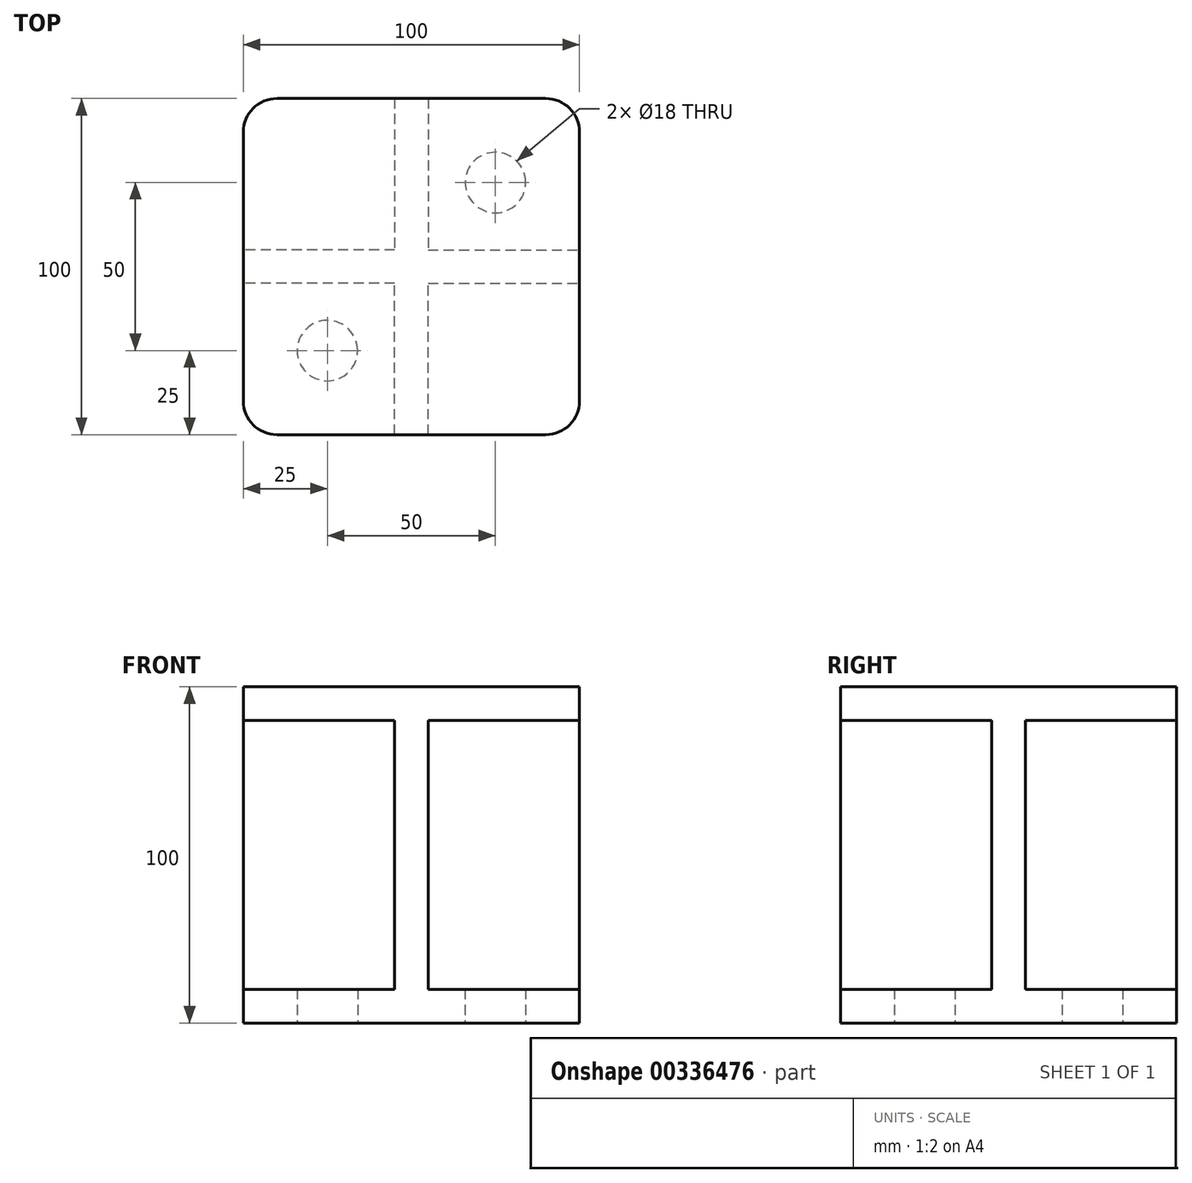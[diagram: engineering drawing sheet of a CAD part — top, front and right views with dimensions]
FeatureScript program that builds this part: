
annotation { "Feature Type Name" : "Feature", "Feature Type Description" : "" }
export const myFeature = defineFeature(function(context is Context, id is Id, definition is map)
    precondition{}
    {
        {
            var Q0;
            Q0=qCreatedBy(makeId("Top.planeOp"),FACE);
            var sketch = newSketch(context, id + "F0", { "sketchPlane" : qUnion([Q0])});
            skLineSegment(sketch, "E0", {"start": v(0, -50) * mm, "end": v(5, -50) * mm});
            skLineSegment(sketch, "E1", {"start": v(5, -50) * mm, "end": v(5, -5) * mm});
            skLineSegment(sketch, "E2", {"start": v(5, -5) * mm, "end": v(50, -5) * mm});
            skLineSegment(sketch, "E3", {"start": v(50, -5) * mm, "end": v(50, 0) * mm});
            skLineSegment(sketch, "E4.MirrorCS", {"start": v(50, 5) * mm, "end": v(50, 0) * mm});
            skLineSegment(sketch, "E5.MirrorCS", {"start": v(5, 5) * mm, "end": v(50, 5) * mm});
            skLineSegment(sketch, "E6.MirrorCS", {"start": v(5, 50) * mm, "end": v(5, 5) * mm});
            skLineSegment(sketch, "E7.MirrorCS", {"start": v(0, 50) * mm, "end": v(5, 50) * mm});
            skLineSegment(sketch, "E8.MirrorCS", {"start": v(0, 50) * mm, "end": v(-5, 50) * mm});
            skLineSegment(sketch, "E9.MirrorCS", {"start": v(-5, 50) * mm, "end": v(-5, 5) * mm});
            skLineSegment(sketch, "E10.MirrorCS", {"start": v(-5, 5) * mm, "end": v(-50, 5) * mm});
            skLineSegment(sketch, "E11.MirrorCS", {"start": v(-50, 5) * mm, "end": v(-50, 0) * mm});
            skLineSegment(sketch, "E12.MirrorCS", {"start": v(-50, -5) * mm, "end": v(-50, 0) * mm});
            skLineSegment(sketch, "E13.MirrorCS", {"start": v(-5, -5) * mm, "end": v(-50, -5) * mm});
            skLineSegment(sketch, "E14.MirrorCS", {"start": v(-5, -50) * mm, "end": v(-5, -5) * mm});
            skLineSegment(sketch, "E15.MirrorCS", {"start": v(0, -50) * mm, "end": v(-5, -50) * mm});
            skSolve(sketch);
        }
        {
            var Q0;
            Q0=makeQuery(id+"F0.imprint","IMPRINT",FACE,{"disambiguationData":[TD([[makeQuery(id+"F0.imprint","IMPRINT",EDGE,{"derivedFrom":sQuery(id+"F0.wireOp",EDGE,"E0")}),1.0]])]});
            extrude(context, id + "F1", {"entities" : qUnion([Q0]), "depth" : 100 * mm});
        }
        {
            var Q0;
            Q0=qCreatedBy(makeId("Top.planeOp"),FACE);
            var sketch = newSketch(context, id + "F2", { "sketchPlane" : qUnion([Q0])});
            skLineSegment(sketch, "E16.bottom", {"start": v(-50, -50) * mm, "end": v(50, -50) * mm});
            skLineSegment(sketch, "E16.top", {"start": v(-50, 50) * mm, "end": v(50, 50) * mm});
            skLineSegment(sketch, "E16.left", {"start": v(-50, -50) * mm, "end": v(-50, 50) * mm});
            skLineSegment(sketch, "E16.right", {"start": v(50, -50) * mm, "end": v(50, 50) * mm});
            skSolve(sketch);
        }
        {
            var Q0;
            Q0=makeQuery(id+"F2.imprint","IMPRINT",FACE,{"disambiguationData":[TD([[makeQuery(id+"F2.imprint","IMPRINT",EDGE,{"derivedFrom":sQuery(id+"F2.wireOp",EDGE,"E16.bottom")}),1.0]])]});
            extrude(context, id + "F3", {"entities" : qUnion([Q0]), "operationType" : NewBodyOperationType.ADD, "depth" : 10 * mm});
        }
        {
            var Q0;
            Q0=makeQuery(id+"F1.opExtrude","CAP_FACE",FACE,{"disambiguationData":[OSD([sQuery(id+"F0.wireOp",EDGE,"E0"),sQuery(id+"F0.wireOp",EDGE,"E1"),sQuery(id+"F0.wireOp",EDGE,"E2"),sQuery(id+"F0.wireOp",EDGE,"E3"),sQuery(id+"F0.wireOp",EDGE,"E4.MirrorCS"),sQuery(id+"F0.wireOp",EDGE,"E5.MirrorCS"),sQuery(id+"F0.wireOp",EDGE,"E6.MirrorCS"),sQuery(id+"F0.wireOp",EDGE,"E7.MirrorCS"),sQuery(id+"F0.wireOp",EDGE,"E8.MirrorCS"),sQuery(id+"F0.wireOp",EDGE,"E9.MirrorCS"),sQuery(id+"F0.wireOp",EDGE,"E10.MirrorCS"),sQuery(id+"F0.wireOp",EDGE,"E11.MirrorCS"),sQuery(id+"F0.wireOp",EDGE,"E12.MirrorCS"),sQuery(id+"F0.wireOp",EDGE,"E13.MirrorCS"),sQuery(id+"F0.wireOp",EDGE,"E14.MirrorCS"),sQuery(id+"F0.wireOp",EDGE,"E15.MirrorCS")])],"isStart":false});
            var sketch = newSketch(context, id + "F4", { "sketchPlane" : qUnion([Q0])});
            skLineSegment(sketch, "E17.bottom", {"start": v(-50, 50) * mm, "end": v(50, 50) * mm});
            skLineSegment(sketch, "E17.top", {"start": v(-50, -50) * mm, "end": v(50, -50) * mm});
            skLineSegment(sketch, "E17.left", {"start": v(-50, 50) * mm, "end": v(-50, -50) * mm});
            skLineSegment(sketch, "E17.right", {"start": v(50, 50) * mm, "end": v(50, -50) * mm});
            skSolve(sketch);
        }
        {
            var Q0;
            {var subQ1=makeQuery(id+"F1.opExtrude","CAP_EDGE",EDGE,{"disambiguationData":[OSD([sQuery(id+"F0.wireOp",EDGE,"E9.MirrorCS")])],"isStart":false});Q0=makeQuery(id+"F4.imprint","IMPRINT",FACE,{"disambiguationData":[TD([[makeQuery(id+"F4.imprint","IMPRINT",EDGE,{"derivedFrom":subQ1}),-1.0]])]});}
            var Q1;
            {var subQ4=makeQuery(id+"F1.opExtrude","CAP_EDGE",EDGE,{"disambiguationData":[OSD([sQuery(id+"F0.wireOp",EDGE,"E1")])],"isStart":false});Q1=makeQuery(id+"F4.imprint","IMPRINT",FACE,{"disambiguationData":[TD([[makeQuery(id+"F4.imprint","IMPRINT",EDGE,{"derivedFrom":subQ4}),1.0]])]});}
            var Q2;
            {var subQ4=makeQuery(id+"F1.opExtrude","CAP_EDGE",EDGE,{"disambiguationData":[OSD([sQuery(id+"F0.wireOp",EDGE,"E5.MirrorCS")])],"isStart":false});Q2=makeQuery(id+"F4.imprint","IMPRINT",FACE,{"disambiguationData":[TD([[makeQuery(id+"F4.imprint","IMPRINT",EDGE,{"derivedFrom":subQ4}),1.0]])]});}
            var Q3;
            {var subQ1=makeQuery(id+"F1.opExtrude","CAP_EDGE",EDGE,{"disambiguationData":[OSD([sQuery(id+"F0.wireOp",EDGE,"E1")])],"isStart":false});Q3=makeQuery(id+"F4.imprint","IMPRINT",FACE,{"disambiguationData":[TD([[makeQuery(id+"F4.imprint","IMPRINT",EDGE,{"derivedFrom":subQ1}),-1.0]])]});}
            var Q4;
            {var subQ4=makeQuery(id+"F1.opExtrude","CAP_EDGE",EDGE,{"disambiguationData":[OSD([sQuery(id+"F0.wireOp",EDGE,"E13.MirrorCS")])],"isStart":false});Q4=makeQuery(id+"F4.imprint","IMPRINT",FACE,{"disambiguationData":[TD([[makeQuery(id+"F4.imprint","IMPRINT",EDGE,{"derivedFrom":subQ4}),1.0]])]});}
            extrude(context, id + "F5", {"entities" : qUnion([Q0, Q1, Q2, Q3, Q4]), "operationType" : NewBodyOperationType.ADD, "oppositeDirection" : true, "depth" : 10 * mm});
        }
        {
            var Q0;
            Q0=makeQuery(id+"F5.opExtrude","SWEPT_EDGE",EDGE,{"disambiguationData":[OSD([sQuery(id+"F4.wireOp",EDGE,"E17.top"),sQuery(id+"F4.wireOp",EDGE,"E17.right")])]});
            var Q1;
            Q1=makeQuery(id+"F3.opExtrude","SWEPT_EDGE",EDGE,{"disambiguationData":[OSD([sQuery(id+"F2.wireOp",EDGE,"E16.bottom"),sQuery(id+"F2.wireOp",EDGE,"E16.right")])]});
            var Q2;
            Q2=makeQuery(id+"F5.opExtrude","SWEPT_EDGE",EDGE,{"disambiguationData":[OSD([sQuery(id+"F4.wireOp",EDGE,"E17.bottom"),sQuery(id+"F4.wireOp",EDGE,"E17.right")])]});
            var Q3;
            Q3=makeQuery(id+"F3.opExtrude","SWEPT_EDGE",EDGE,{"disambiguationData":[OSD([sQuery(id+"F2.wireOp",EDGE,"E16.top"),sQuery(id+"F2.wireOp",EDGE,"E16.right")])]});
            var Q4;
            Q4=makeQuery(id+"F5.opExtrude","SWEPT_EDGE",EDGE,{"disambiguationData":[OSD([sQuery(id+"F4.wireOp",EDGE,"E17.top"),sQuery(id+"F4.wireOp",EDGE,"E17.left")])]});
            var Q5;
            Q5=makeQuery(id+"F3.opExtrude","SWEPT_EDGE",EDGE,{"disambiguationData":[OSD([sQuery(id+"F2.wireOp",EDGE,"E16.bottom"),sQuery(id+"F2.wireOp",EDGE,"E16.left")])]});
            var Q6;
            Q6=makeQuery(id+"F5.opExtrude","SWEPT_EDGE",EDGE,{"disambiguationData":[OSD([sQuery(id+"F4.wireOp",EDGE,"E17.bottom"),sQuery(id+"F4.wireOp",EDGE,"E17.left")])]});
            var Q7;
            Q7=makeQuery(id+"F3.opExtrude","SWEPT_EDGE",EDGE,{"disambiguationData":[OSD([sQuery(id+"F2.wireOp",EDGE,"E16.top"),sQuery(id+"F2.wireOp",EDGE,"E16.left")])]});
            fillet(context, id + "F6", {"entities" : qUnion([Q0, Q1, Q2, Q3, Q4, Q5, Q6, Q7]), "radius" : 10 * mm, "tangentPropagation" : true, "allowEdgeOverflow" : false});
        }
        {
            var Q0;
            Q0=qCreatedBy(makeId("Top.planeOp"),FACE);
            var sketch = newSketch(context, id + "F7", { "sketchPlane" : qUnion([Q0])});
            skCircle(sketch, "E18.0.1.0", {"center": v(-25, -25) * mm, "radius": 9 * mm});
            skCircle(sketch, "E18.1.0.0", {"center": v(25, 25) * mm, "radius": 9 * mm});
            skLineSegment(sketch, "E18.direction1", {"start": v(-25, 25) * mm, "end": v(25, 25) * mm, "construction": true});
            skLineSegment(sketch, "E18.direction2", {"start": v(-25, 25) * mm, "end": v(-25, -25) * mm, "construction": true});
            skSolve(sketch);
        }
        {
            var Q0;
            Q0 = qSketchRegion(id + "F7", true);
            extrude(context, id + "F8", {"entities" : qUnion([Q0]), "operationType" : NewBodyOperationType.REMOVE, "endBound" : BoundingType.SYMMETRIC, "depth" : 174 * mm});
        }
    });
